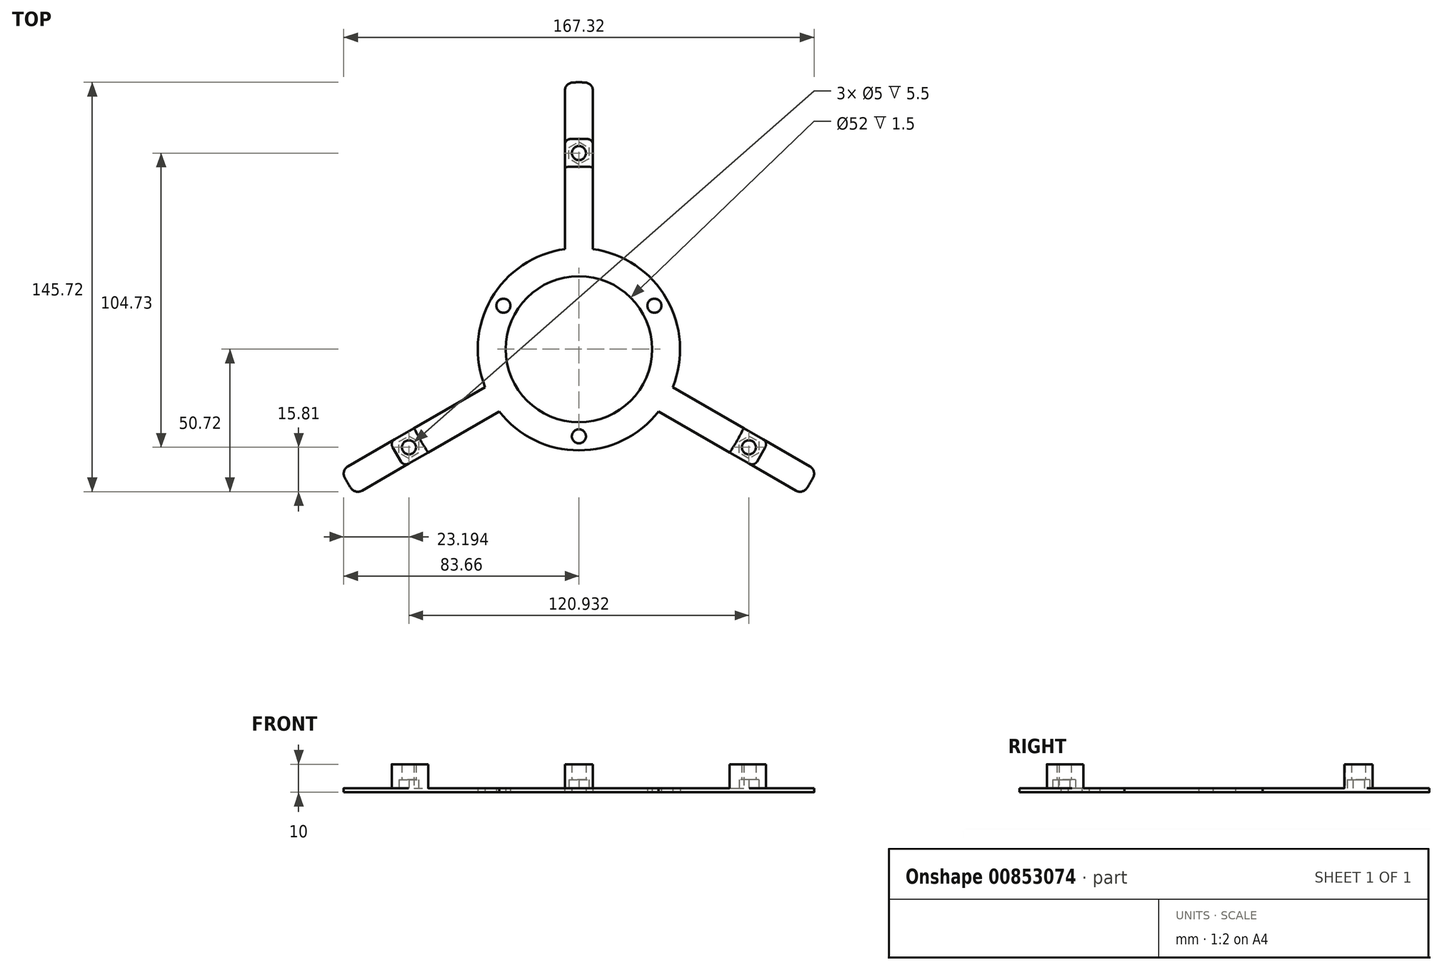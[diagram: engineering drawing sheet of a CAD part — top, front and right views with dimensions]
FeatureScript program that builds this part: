
annotation { "Feature Type Name" : "Feature", "Feature Type Description" : "" }
export const myFeature = defineFeature(function(context is Context, id is Id, definition is map)
    precondition{}
    {
        {
            var Q0;
            Q0=qCreatedBy(makeId("Top.planeOp"),FACE);
            var sketch = newSketch(context, id + "F0", { "sketchPlane" : qUnion([Q0])});
            skCircle(sketch, "E0", {"center": v(0, 0) * mm, "radius": 26 * mm});
            skLineSegment(sketch, "E1", {"start": v(0, 0) * mm, "end": v(0, 26) * mm, "construction": true});
            skLineSegment(sketch, "E2", {"start": v(0, 26) * mm, "end": v(0, 75) * mm, "construction": true});
            skLineSegment(sketch, "E3", {"start": v(0, 0) * mm, "end": v(22.52, -13) * mm, "construction": true});
            skLineSegment(sketch, "E4", {"start": v(22.52, -13) * mm, "end": v(64.95, -37.5) * mm, "construction": true});
            skLineSegment(sketch, "E5", {"start": v(0, 0) * mm, "end": v(-22.52, -13) * mm, "construction": true});
            skLineSegment(sketch, "E6", {"start": v(-22.52, -13) * mm, "end": v(-64.95, -37.5) * mm, "construction": true});
            skLineSegment(sketch, "E7", {"start": v(-5, 25.51) * mm, "end": v(-5, 74.83) * mm});
            skLineSegment(sketch, "E8", {"start": v(-5, 74.83) * mm, "end": v(5, 74.83) * mm});
            skLineSegment(sketch, "E9", {"start": v(5, 74.83) * mm, "end": v(5, 25.51) * mm});
            skLineSegment(sketch, "E10", {"start": v(24.6, -8.43) * mm, "end": v(67.3, -33.09) * mm});
            skLineSegment(sketch, "E11", {"start": v(67.3, -33.09) * mm, "end": v(62.3, -41.75) * mm});
            skLineSegment(sketch, "E12", {"start": v(62.3, -41.75) * mm, "end": v(19.6, -17.09) * mm});
            skLineSegment(sketch, "E13", {"start": v(-19.6, -17.09) * mm, "end": v(-62.3, -41.75) * mm});
            skLineSegment(sketch, "E14", {"start": v(-62.3, -41.75) * mm, "end": v(-67.3, -33.09) * mm});
            skLineSegment(sketch, "E15", {"start": v(-67.3, -33.09) * mm, "end": v(-24.6, -8.43) * mm});
            skCircle(sketch, "E16", {"center": v(0, 0) * mm, "radius": 75 * mm});
            skCircle(sketch, "E17", {"center": v(0, 0) * mm, "radius": 95 * mm});
            skCircle(sketch, "E18", {"center": v(0, 0) * mm, "radius": 36 * mm});
            skCircle(sketch, "E19", {"center": v(0, 0) * mm, "radius": 65 * mm});
            skLineSegment(sketch, "E20", {"start": v(-5, 74.83) * mm, "end": v(5, 64.8) * mm, "construction": true});
            skLineSegment(sketch, "E21", {"start": v(5, 74.83) * mm, "end": v(-5, 64.8) * mm, "construction": true});
            skLineSegment(sketch, "E22", {"start": v(-62.3, -41.75) * mm, "end": v(-58.62, -28.07) * mm, "construction": true});
            skLineSegment(sketch, "E23", {"start": v(62.3, -41.75) * mm, "end": v(58.62, -28.07) * mm, "construction": true});
            skCircle(sketch, "E24", {"center": v(-60.47, -34.91) * mm, "radius": 2.5 * mm});
            skCircle(sketch, "E25", {"center": v(60.47, -34.91) * mm, "radius": 2.5 * mm});
            skCircle(sketch, "E26", {"center": v(0, 69.82) * mm, "radius": 2.5 * mm});
            skLineSegment(sketch, "E27", {"start": v(0, 0) * mm, "end": v(56.3, 32.5) * mm, "construction": true});
            skLineSegment(sketch, "E28", {"start": v(56.3, 32.5) * mm, "end": v(64.95, 37.5) * mm, "construction": true});
            skLineSegment(sketch, "E29", {"start": v(0, 0) * mm, "end": v(0, -65) * mm, "construction": true});
            skLineSegment(sketch, "E30", {"start": v(0, -65) * mm, "end": v(0, -75) * mm, "construction": true});
            skLineSegment(sketch, "E31", {"start": v(0, 0) * mm, "end": v(-56.3, 32.5) * mm, "construction": true});
            skLineSegment(sketch, "E32", {"start": v(-56.3, 32.5) * mm, "end": v(-64.95, 37.5) * mm, "construction": true});
            skCircle(sketch, "E33", {"center": v(-60.62, 35) * mm, "radius": 2.5 * mm});
            skCircle(sketch, "E34", {"center": v(0, -70) * mm, "radius": 2.5 * mm});
            skPoint(sketch, "E34.perimeterSnap0", {"position": v(0, -70) * mm});
            skCircle(sketch, "E35", {"center": v(60.62, 35) * mm, "radius": 2.5 * mm});
            skLineSegment(sketch, "E36", {"start": v(-67.3, -33.09) * mm, "end": v(-84.66, -43.1) * mm});
            skLineSegment(sketch, "E37", {"start": v(-62.3, -41.75) * mm, "end": v(-79.66, -51.76) * mm});
            skLineSegment(sketch, "E38", {"start": v(62.3, -41.75) * mm, "end": v(79.66, -51.76) * mm});
            skLineSegment(sketch, "E39", {"start": v(67.3, -33.09) * mm, "end": v(84.66, -43.1) * mm});
            skLineSegment(sketch, "E40", {"start": v(5, 74.83) * mm, "end": v(5, 94.87) * mm});
            skLineSegment(sketch, "E41", {"start": v(-5, 74.83) * mm, "end": v(-5, 94.87) * mm});
            skCircle(sketch, "E42.cCircle", {"center": v(-60.47, -34.91) * mm, "radius": 3.5 * mm, "construction": true});
            skLineSegment(sketch, "E42.0", {"start": v(-60.47, -30.87) * mm, "end": v(-56.97, -32.89) * mm});
            skLineSegment(sketch, "E42.1", {"start": v(-56.97, -32.89) * mm, "end": v(-56.97, -36.93) * mm});
            skLineSegment(sketch, "E42.2", {"start": v(-56.97, -36.93) * mm, "end": v(-60.47, -38.95) * mm});
            skLineSegment(sketch, "E42.3", {"start": v(-60.47, -38.95) * mm, "end": v(-63.97, -36.93) * mm});
            skLineSegment(sketch, "E42.4", {"start": v(-63.97, -36.93) * mm, "end": v(-63.97, -32.89) * mm});
            skLineSegment(sketch, "E42.5", {"start": v(-63.97, -32.89) * mm, "end": v(-60.47, -30.87) * mm});
            skPoint(sketch, "E42.0.midPoint", {"position": v(-58.72, -31.88) * mm});
            skLineSegment(sketch, "E43.1.0", {"start": v(60.47, -38.95) * mm, "end": v(56.97, -36.93) * mm});
            skLineSegment(sketch, "E43.1.1", {"start": v(56.97, -36.93) * mm, "end": v(56.97, -32.89) * mm});
            skLineSegment(sketch, "E43.1.2", {"start": v(56.97, -32.89) * mm, "end": v(60.47, -30.87) * mm});
            skLineSegment(sketch, "E43.1.3", {"start": v(60.47, -30.87) * mm, "end": v(63.97, -32.89) * mm});
            skLineSegment(sketch, "E43.1.4", {"start": v(63.97, -32.89) * mm, "end": v(63.97, -36.93) * mm});
            skLineSegment(sketch, "E43.1.5", {"start": v(63.97, -36.93) * mm, "end": v(60.47, -38.95) * mm});
            skLineSegment(sketch, "E43.2.0", {"start": v(3.5, 71.84) * mm, "end": v(3.5, 67.8) * mm});
            skLineSegment(sketch, "E43.2.1", {"start": v(3.5, 67.8) * mm, "end": v(0, 65.78) * mm});
            skLineSegment(sketch, "E43.2.2", {"start": v(0, 65.78) * mm, "end": v(-3.5, 67.8) * mm});
            skLineSegment(sketch, "E43.2.3", {"start": v(-3.5, 67.8) * mm, "end": v(-3.5, 71.84) * mm});
            skLineSegment(sketch, "E43.2.4", {"start": v(-3.5, 71.84) * mm, "end": v(0, 73.86) * mm});
            skLineSegment(sketch, "E43.2.5", {"start": v(0, 73.86) * mm, "end": v(3.5, 71.84) * mm});
            skCircle(sketch, "E44", {"center": v(26.85, 15.5) * mm, "radius": 5 * mm, "construction": true});
            skCircle(sketch, "E45", {"center": v(-26.85, 15.5) * mm, "radius": 5 * mm, "construction": true});
            skCircle(sketch, "E46", {"center": v(0, -31) * mm, "radius": 5 * mm, "construction": true});
            skCircle(sketch, "E47", {"center": v(-26.85, 15.5) * mm, "radius": 2.5 * mm});
            skCircle(sketch, "E48", {"center": v(26.85, 15.5) * mm, "radius": 2.5 * mm});
            skCircle(sketch, "E49", {"center": v(0, -31) * mm, "radius": 2.5 * mm});
            skSolve(sketch);
        }
        {
            var Q0;
            {var subQ3=sQuery(id+"F0.wireOp",EDGE,"E38");Q0=makeQuery(id+"F0.imprint","IMPRINT",FACE,{"disambiguationData":[TD([[makeQuery(id+"F0.imprint","IMPRINT",EDGE,{"derivedFrom":subQ3}),1.0]])]});}
            var Q1;
            {var subQ0=sQuery(id+"F0.wireOp",EDGE,"E11");Q1=makeQuery(id+"F0.imprint","IMPRINT",FACE,{"disambiguationData":[TD([[makeQuery(id+"F0.imprint","IMPRINT",EDGE,{"derivedFrom":subQ0}),1.0]])]});}
            var Q2;
            {var subQ5=sQuery(id+"F0.wireOp",EDGE,"E11");Q2=makeQuery(id+"F0.imprint","IMPRINT",FACE,{"disambiguationData":[TD([[makeQuery(id+"F0.imprint","IMPRINT",EDGE,{"derivedFrom":subQ5}),-1.0]])]});}
            var Q3;
            {var subQ0=sQuery(id+"F0.wireOp",EDGE,"E18");var subQ1=sQuery(id+"F0.wireOp",EDGE,"E10");var subQ2=makeQuery(id+"F0.imprint","INTERSECT",VERTEX,{"derivedFrom":[subQ1,subQ0]});Q3=makeQuery(id+"F0.imprint","IMPRINT",FACE,{"disambiguationData":[TD([[makeQuery(id+"F0.imprint","IMPRINT",EDGE,{"disambiguationData":[TD([[subQ2,-1.0]])],"derivedFrom":subQ1}),-1.0]])]});}
            var Q4;
            {var subQ0=sQuery(id+"F0.wireOp",EDGE,"E10");var subQ1=sQuery(id+"F0.wireOp",EDGE,"E0");var subQ2=makeQuery(id+"F0.imprint","INTERSECT",VERTEX,{"derivedFrom":[subQ1,subQ0]});Q4=makeQuery(id+"F0.imprint","IMPRINT",FACE,{"disambiguationData":[TD([[makeQuery(id+"F0.imprint","IMPRINT",EDGE,{"disambiguationData":[TD([[subQ2,1.0]])],"derivedFrom":subQ1}),-1.0]])]});}
            var Q5;
            {var subQ0=sQuery(id+"F0.wireOp",EDGE,"E9");var subQ1=sQuery(id+"F0.wireOp",EDGE,"E0");var subQ2=makeQuery(id+"F0.imprint","INTERSECT",VERTEX,{"derivedFrom":[subQ1,subQ0]});Q5=makeQuery(id+"F0.imprint","IMPRINT",FACE,{"disambiguationData":[TD([[makeQuery(id+"F0.imprint","IMPRINT",EDGE,{"disambiguationData":[TD([[subQ2,1.0]])],"derivedFrom":subQ1}),-1.0]])]});}
            var Q6;
            {var subQ0=sQuery(id+"F0.wireOp",EDGE,"E12");var subQ1=sQuery(id+"F0.wireOp",EDGE,"E0");var subQ2=makeQuery(id+"F0.imprint","INTERSECT",VERTEX,{"derivedFrom":[subQ1,subQ0]});Q6=makeQuery(id+"F0.imprint","IMPRINT",FACE,{"disambiguationData":[TD([[makeQuery(id+"F0.imprint","IMPRINT",EDGE,{"disambiguationData":[TD([[subQ2,1.0]])],"derivedFrom":subQ1}),-1.0]])]});}
            var Q7;
            {var subQ0=sQuery(id+"F0.wireOp",EDGE,"E18");var subQ1=sQuery(id+"F0.wireOp",EDGE,"E13");var subQ2=makeQuery(id+"F0.imprint","INTERSECT",VERTEX,{"derivedFrom":[subQ1,subQ0]});Q7=makeQuery(id+"F0.imprint","IMPRINT",FACE,{"disambiguationData":[TD([[makeQuery(id+"F0.imprint","IMPRINT",EDGE,{"disambiguationData":[TD([[subQ2,-1.0]])],"derivedFrom":subQ1}),-1.0]])]});}
            var Q8;
            {var subQ0=sQuery(id+"F0.wireOp",EDGE,"E13");var subQ1=sQuery(id+"F0.wireOp",EDGE,"E0");var subQ2=makeQuery(id+"F0.imprint","INTERSECT",VERTEX,{"derivedFrom":[subQ1,subQ0]});Q8=makeQuery(id+"F0.imprint","IMPRINT",FACE,{"disambiguationData":[TD([[makeQuery(id+"F0.imprint","IMPRINT",EDGE,{"disambiguationData":[TD([[subQ2,1.0]])],"derivedFrom":subQ1}),-1.0]])]});}
            var Q9;
            {var subQ2=sQuery(id+"F0.wireOp",EDGE,"E14");Q9=makeQuery(id+"F0.imprint","IMPRINT",FACE,{"disambiguationData":[TD([[makeQuery(id+"F0.imprint","IMPRINT",EDGE,{"derivedFrom":subQ2}),-1.0]])]});}
            var Q10;
            {var subQ0=sQuery(id+"F0.wireOp",EDGE,"E14");Q10=makeQuery(id+"F0.imprint","IMPRINT",FACE,{"disambiguationData":[TD([[makeQuery(id+"F0.imprint","IMPRINT",EDGE,{"derivedFrom":subQ0}),1.0]])]});}
            var Q11;
            {var subQ3=sQuery(id+"F0.wireOp",EDGE,"E36");Q11=makeQuery(id+"F0.imprint","IMPRINT",FACE,{"disambiguationData":[TD([[makeQuery(id+"F0.imprint","IMPRINT",EDGE,{"derivedFrom":subQ3}),1.0]])]});}
            var Q12;
            {var subQ0=sQuery(id+"F0.wireOp",EDGE,"E7");var subQ1=sQuery(id+"F0.wireOp",EDGE,"E0");var subQ2=makeQuery(id+"F0.imprint","INTERSECT",VERTEX,{"derivedFrom":[subQ1,subQ0]});Q12=makeQuery(id+"F0.imprint","IMPRINT",FACE,{"disambiguationData":[TD([[makeQuery(id+"F0.imprint","IMPRINT",EDGE,{"disambiguationData":[TD([[subQ2,-1.0]])],"derivedFrom":subQ1}),-1.0]])]});}
            var Q13;
            {var subQ0=sQuery(id+"F0.wireOp",EDGE,"E7");var subQ1=sQuery(id+"F0.wireOp",EDGE,"E0");var subQ2=makeQuery(id+"F0.imprint","INTERSECT",VERTEX,{"derivedFrom":[subQ1,subQ0]});Q13=makeQuery(id+"F0.imprint","IMPRINT",FACE,{"disambiguationData":[TD([[makeQuery(id+"F0.imprint","IMPRINT",EDGE,{"disambiguationData":[TD([[subQ2,1.0]])],"derivedFrom":subQ1}),-1.0]])]});}
            var Q14;
            {var subQ0=sQuery(id+"F0.wireOp",EDGE,"E18");var subQ1=sQuery(id+"F0.wireOp",EDGE,"E7");var subQ2=makeQuery(id+"F0.imprint","INTERSECT",VERTEX,{"derivedFrom":[subQ1,subQ0]});Q14=makeQuery(id+"F0.imprint","IMPRINT",FACE,{"disambiguationData":[TD([[makeQuery(id+"F0.imprint","IMPRINT",EDGE,{"disambiguationData":[TD([[subQ2,-1.0]])],"derivedFrom":subQ1}),-1.0]])]});}
            var Q15;
            {var subQ6=sQuery(id+"F0.wireOp",EDGE,"E8");Q15=makeQuery(id+"F0.imprint","IMPRINT",FACE,{"disambiguationData":[TD([[makeQuery(id+"F0.imprint","IMPRINT",EDGE,{"derivedFrom":subQ6}),-1.0]])]});}
            var Q16;
            {var subQ0=sQuery(id+"F0.wireOp",EDGE,"E8");Q16=makeQuery(id+"F0.imprint","IMPRINT",FACE,{"disambiguationData":[TD([[makeQuery(id+"F0.imprint","IMPRINT",EDGE,{"derivedFrom":subQ0}),1.0]])]});}
            var Q17;
            {var subQ3=sQuery(id+"F0.wireOp",EDGE,"E40");Q17=makeQuery(id+"F0.imprint","IMPRINT",FACE,{"disambiguationData":[TD([[makeQuery(id+"F0.imprint","IMPRINT",EDGE,{"derivedFrom":subQ3}),1.0]])]});}
            var Q18;
            Q18=makeQuery(id+"F0.imprint","IMPRINT",FACE,{"disambiguationData":[TD([[makeQuery(id+"F0.imprint","IMPRINT",EDGE,{"derivedFrom":sQuery(id+"F0.wireOp",EDGE,"E25")}),-1.0]])]});
            var Q19;
            Q19=makeQuery(id+"F0.imprint","IMPRINT",FACE,{"disambiguationData":[TD([[makeQuery(id+"F0.imprint","IMPRINT",EDGE,{"derivedFrom":sQuery(id+"F0.wireOp",EDGE,"E26")}),-1.0]])]});
            var Q20;
            Q20=makeQuery(id+"F0.imprint","IMPRINT",FACE,{"disambiguationData":[TD([[makeQuery(id+"F0.imprint","IMPRINT",EDGE,{"derivedFrom":sQuery(id+"F0.wireOp",EDGE,"E24")}),-1.0]])]});
            extrude(context, id + "F1", {"entities" : qUnion([Q0, Q1, Q2, Q3, Q4, Q5, Q6, Q7, Q8, Q9, Q10, Q11, Q12, Q13, Q14, Q15, Q16, Q17, Q18, Q19, Q20]), "depth" : 1.5 * mm, "offsetDistance" : 25 * mm});
        }
        {
            var Q0;
            {var subQ2=sQuery(id+"F0.wireOp",EDGE,"E14");Q0=makeQuery(id+"F0.imprint","IMPRINT",FACE,{"disambiguationData":[TD([[makeQuery(id+"F0.imprint","IMPRINT",EDGE,{"derivedFrom":subQ2}),-1.0]])]});}
            var Q1;
            {var subQ6=sQuery(id+"F0.wireOp",EDGE,"E8");Q1=makeQuery(id+"F0.imprint","IMPRINT",FACE,{"disambiguationData":[TD([[makeQuery(id+"F0.imprint","IMPRINT",EDGE,{"derivedFrom":subQ6}),-1.0]])]});}
            var Q2;
            {var subQ5=sQuery(id+"F0.wireOp",EDGE,"E11");Q2=makeQuery(id+"F0.imprint","IMPRINT",FACE,{"disambiguationData":[TD([[makeQuery(id+"F0.imprint","IMPRINT",EDGE,{"derivedFrom":subQ5}),-1.0]])]});}
            var Q3;
            Q3=makeQuery(id+"F0.imprint","IMPRINT",FACE,{"disambiguationData":[TD([[makeQuery(id+"F0.imprint","IMPRINT",EDGE,{"derivedFrom":sQuery(id+"F0.wireOp",EDGE,"E24")}),-1.0]])]});
            var Q4;
            Q4=makeQuery(id+"F0.imprint","IMPRINT",FACE,{"disambiguationData":[TD([[makeQuery(id+"F0.imprint","IMPRINT",EDGE,{"derivedFrom":sQuery(id+"F0.wireOp",EDGE,"E25")}),-1.0]])]});
            var Q5;
            Q5=makeQuery(id+"F0.imprint","IMPRINT",FACE,{"disambiguationData":[TD([[makeQuery(id+"F0.imprint","IMPRINT",EDGE,{"derivedFrom":sQuery(id+"F0.wireOp",EDGE,"E26")}),-1.0]])]});
            extrude(context, id + "F2", {"entities" : qUnion([Q0, Q1, Q2, Q3, Q4, Q5]), "operationType" : NewBodyOperationType.ADD, "depth" : 10 * mm, "offsetDistance" : 25 * mm});
        }
        {
            var Q0;
            Q0=makeQuery(id+"F2.opExtrude","SWEPT_EDGE",EDGE,{"disambiguationData":[OSD([sQuery(id+"F0.wireOp",EDGE,"E10"),sQuery(id+"F0.wireOp",EDGE,"E11"),sQuery(id+"F0.wireOp",EDGE,"E16"),sQuery(id+"F0.wireOp",EDGE,"E39")])]});
            var Q1;
            Q1=makeQuery(id+"F2.opExtrude","SWEPT_EDGE",EDGE,{"disambiguationData":[OSD([sQuery(id+"F0.wireOp",EDGE,"E11"),sQuery(id+"F0.wireOp",EDGE,"E12"),sQuery(id+"F0.wireOp",EDGE,"E16"),sQuery(id+"F0.wireOp",EDGE,"E38")])]});
            var Q2;
            Q2=makeQuery(id+"F2.opExtrude","SWEPT_EDGE",EDGE,{"disambiguationData":[OSD([sQuery(id+"F0.wireOp",EDGE,"E13"),sQuery(id+"F0.wireOp",EDGE,"E14"),sQuery(id+"F0.wireOp",EDGE,"E16"),sQuery(id+"F0.wireOp",EDGE,"E37")])]});
            var Q3;
            Q3=makeQuery(id+"F2.opExtrude","SWEPT_EDGE",EDGE,{"disambiguationData":[OSD([sQuery(id+"F0.wireOp",EDGE,"E14"),sQuery(id+"F0.wireOp",EDGE,"E15"),sQuery(id+"F0.wireOp",EDGE,"E16"),sQuery(id+"F0.wireOp",EDGE,"E36")])]});
            var Q4;
            Q4=makeQuery(id+"F2.opExtrude","SWEPT_EDGE",EDGE,{"disambiguationData":[OSD([sQuery(id+"F0.wireOp",EDGE,"E8"),sQuery(id+"F0.wireOp",EDGE,"E9"),sQuery(id+"F0.wireOp",EDGE,"E16"),sQuery(id+"F0.wireOp",EDGE,"E40")])]});
            var Q5;
            Q5=makeQuery(id+"F2.opExtrude","SWEPT_EDGE",EDGE,{"disambiguationData":[OSD([sQuery(id+"F0.wireOp",EDGE,"E7"),sQuery(id+"F0.wireOp",EDGE,"E8"),sQuery(id+"F0.wireOp",EDGE,"E16"),sQuery(id+"F0.wireOp",EDGE,"E41")])]});
            fillet(context, id + "F3", {"entities" : qUnion([Q0, Q1, Q2, Q3, Q4, Q5]), "radius" : 2 * mm, "tangentPropagation" : true, "allowEdgeOverflow" : false});
        }
        {
            var Q0;
            Q0=makeQuery(id+"F1.opExtrude","SWEPT_EDGE",EDGE,{"disambiguationData":[OSD([sQuery(id+"F0.wireOp",EDGE,"E17"),sQuery(id+"F0.wireOp",EDGE,"E39")])]});
            var Q1;
            Q1=makeQuery(id+"F1.opExtrude","SWEPT_EDGE",EDGE,{"disambiguationData":[OSD([sQuery(id+"F0.wireOp",EDGE,"E17"),sQuery(id+"F0.wireOp",EDGE,"E38")])]});
            var Q2;
            Q2=makeQuery(id+"F1.opExtrude","SWEPT_EDGE",EDGE,{"disambiguationData":[OSD([sQuery(id+"F0.wireOp",EDGE,"E17"),sQuery(id+"F0.wireOp",EDGE,"E37")])]});
            var Q3;
            Q3=makeQuery(id+"F1.opExtrude","SWEPT_EDGE",EDGE,{"disambiguationData":[OSD([sQuery(id+"F0.wireOp",EDGE,"E17"),sQuery(id+"F0.wireOp",EDGE,"E36")])]});
            var Q4;
            Q4=makeQuery(id+"F1.opExtrude","SWEPT_EDGE",EDGE,{"disambiguationData":[OSD([sQuery(id+"F0.wireOp",EDGE,"E17"),sQuery(id+"F0.wireOp",EDGE,"E41")])]});
            var Q5;
            Q5=makeQuery(id+"F1.opExtrude","SWEPT_EDGE",EDGE,{"disambiguationData":[OSD([sQuery(id+"F0.wireOp",EDGE,"E17"),sQuery(id+"F0.wireOp",EDGE,"E40")])]});
            fillet(context, id + "F4", {"entities" : qUnion([Q0, Q1, Q2, Q3, Q4, Q5]), "radius" : 3 * mm, "tangentPropagation" : true, "allowEdgeOverflow" : false});
        }
        {
            var Q0;
            Q0=makeQuery(id+"F0.imprint","IMPRINT",FACE,{"disambiguationData":[TD([[makeQuery(id+"F0.imprint","IMPRINT",EDGE,{"derivedFrom":sQuery(id+"F0.wireOp",EDGE,"E25")}),-1.0]])]});
            var Q1;
            Q1=makeQuery(id+"F0.imprint","IMPRINT",FACE,{"disambiguationData":[TD([[makeQuery(id+"F0.imprint","IMPRINT",EDGE,{"derivedFrom":sQuery(id+"F0.wireOp",EDGE,"E24")}),-1.0]])]});
            var Q2;
            Q2=makeQuery(id+"F0.imprint","IMPRINT",FACE,{"disambiguationData":[TD([[makeQuery(id+"F0.imprint","IMPRINT",EDGE,{"derivedFrom":sQuery(id+"F0.wireOp",EDGE,"E26")}),-1.0]])]});
            extrude(context, id + "F5", {"entities" : qUnion([Q0, Q1, Q2]), "operationType" : NewBodyOperationType.REMOVE, "depth" : 4.5 * mm, "offsetDistance" : 25 * mm});
        }
    });
